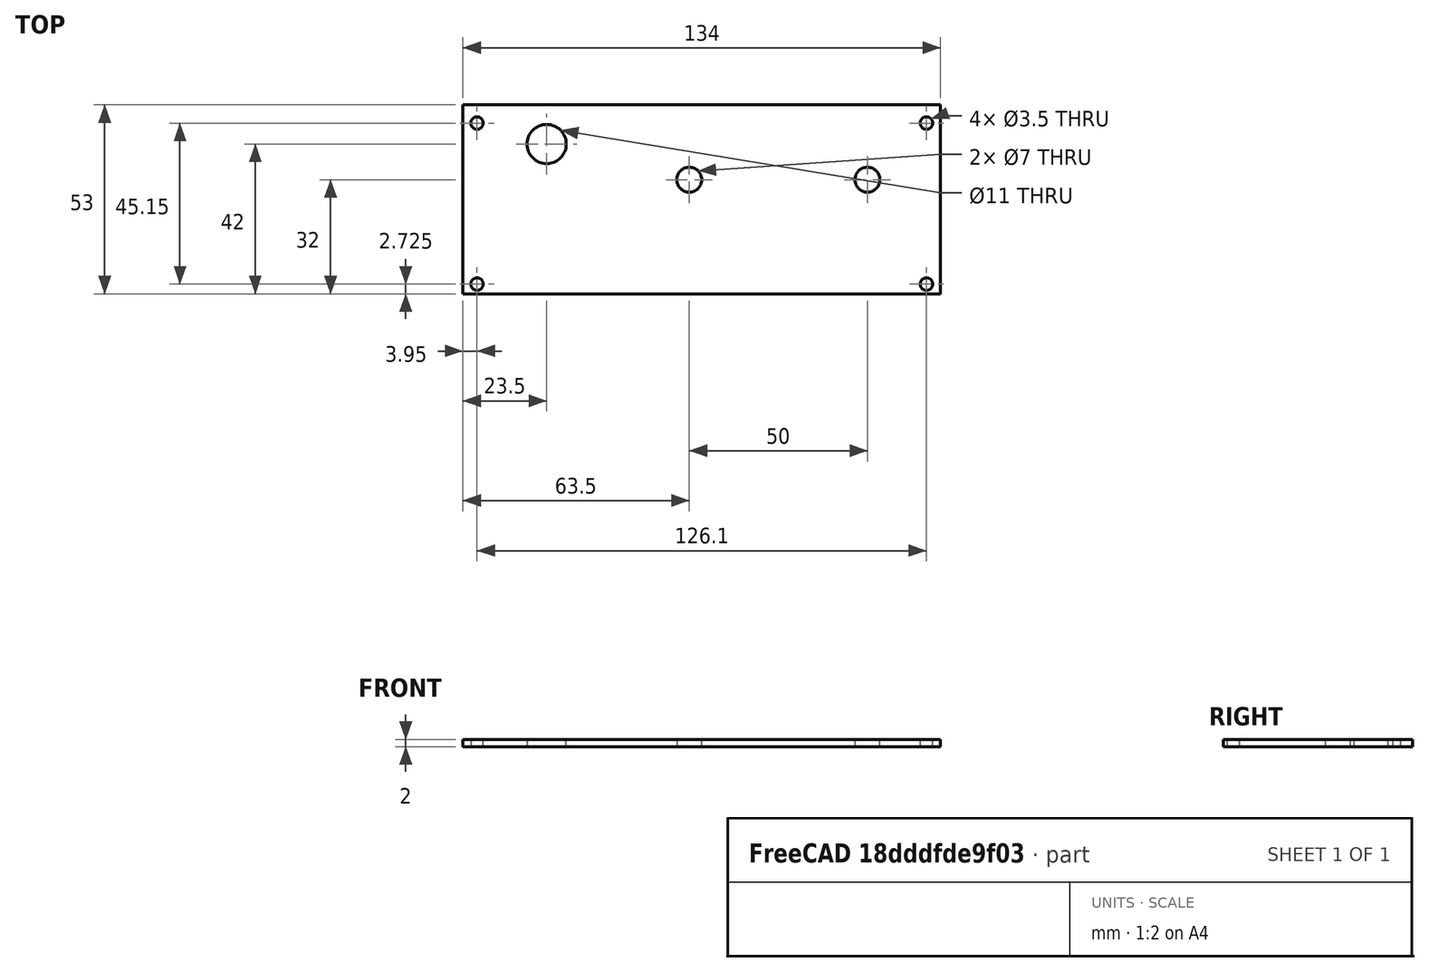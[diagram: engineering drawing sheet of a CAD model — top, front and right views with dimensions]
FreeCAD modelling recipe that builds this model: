
FCSTD DOCUMENT  (FreeCAD 0.20RUnknown)
Label: 端面
License: All rights reserved
LicenseURL: http://en.wikipedia.org/wiki/All_rights_reserved
objects: Sketcher::SketchObject×1, PartDesign::Pad×1, PartDesign::Body×1, TechDraw::DrawSVGTemplate×1, TechDraw::DrawViewPart×1, TechDraw::DrawPage×1
note: 4 computed .brp shape members not serialized (recipe doc carries the construction recipe); baked Part::Feature solids carry a one-line shape summary decoded from their .brp

FEATURE [Sketcher::SketchObject] Sketch
  FullyConstrained = true
  MapMode = 5
  Support = -> [XY_Plane]
  sketch-geometry (35):
    g0: LineSegment StartX=0 StartY=0 StartZ=0 EndX=134 EndY=0 EndZ=0
    g1: LineSegment StartX=134 StartY=0 StartZ=0 EndX=134 EndY=53 EndZ=0
    g2: LineSegment StartX=134 StartY=53 StartZ=0 EndX=0 EndY=53 EndZ=0
    g3: LineSegment StartX=0 StartY=53 StartZ=0 EndX=0 EndY=0 EndZ=0
    g4: LineSegment StartX=2 StartY=0 StartZ=0 EndX=132 EndY=0 EndZ=0
    g5: LineSegment StartX=132 StartY=0 StartZ=0 EndX=132 EndY=50.6 EndZ=0
    g6: LineSegment StartX=132 StartY=50.6 StartZ=0 EndX=2 EndY=50.6 EndZ=0
    g7: LineSegment StartX=2 StartY=50.6 StartZ=0 EndX=2 EndY=0 EndZ=0
    g8: LineSegment StartX=2 StartY=50.6 StartZ=0 EndX=5.9 EndY=50.6 EndZ=0
    g9: LineSegment StartX=5.9 StartY=50.6 StartZ=0 EndX=5.9 EndY=45.15 EndZ=0
    g10: LineSegment StartX=2 StartY=45.15 StartZ=0 EndX=2 EndY=50.6 EndZ=0
    g11: LineSegment StartX=132 StartY=50.6 StartZ=0 EndX=128.1 EndY=50.6 EndZ=0
    g12: LineSegment StartX=128.1 StartY=50.6 StartZ=0 EndX=128.1 EndY=45.15 EndZ=0
    g13: LineSegment StartX=128.1 StartY=45.15 StartZ=0 EndX=132 EndY=45.15 EndZ=0
    g14: LineSegment StartX=132 StartY=45.15 StartZ=0 EndX=132 EndY=50.6 EndZ=0
    g15: LineSegment StartX=132 StartY=0 StartZ=0 EndX=128.1 EndY=0 EndZ=0
    g16: LineSegment StartX=128.1 StartY=0 StartZ=0 EndX=128.1 EndY=5.45 EndZ=0
    g17: LineSegment StartX=128.1 StartY=5.45 StartZ=0 EndX=132 EndY=5.45 EndZ=0
    g18: LineSegment StartX=132 StartY=5.45 StartZ=0 EndX=132 EndY=0 EndZ=0
    g19: LineSegment StartX=2 StartY=0 StartZ=0 EndX=5.9 EndY=0 EndZ=0
    g20: LineSegment StartX=5.9 StartY=0 StartZ=0 EndX=5.9 EndY=5.45 EndZ=0
    g21: LineSegment StartX=5.9 StartY=5.45 StartZ=0 EndX=2 EndY=5.45 EndZ=0
    g22: LineSegment StartX=2 StartY=5.45 StartZ=0 EndX=2 EndY=0 EndZ=0
    g23: GeomPoint X=3.95 Y=47.875 Z=0
    g24: GeomPoint X=3.95 Y=2.725 Z=0
    g25: GeomPoint X=130.05 Y=47.875 Z=0
    g26: GeomPoint X=130.05 Y=2.725 Z=0
    g27: Circle CenterX=3.95 CenterY=47.875 CenterZ=0 NormalX=0 NormalY=0 NormalZ=1 AngleXU=0 Radius=1.75
    g28: Circle CenterX=3.95 CenterY=2.725 CenterZ=0 NormalX=0 NormalY=0 NormalZ=1 AngleXU=0 Radius=1.75
    g29: Circle CenterX=130.05 CenterY=2.725 CenterZ=0 NormalX=0 NormalY=0 NormalZ=1 AngleXU=0 Radius=1.75
    g30: Circle CenterX=130.05 CenterY=47.875 CenterZ=0 NormalX=0 NormalY=0 NormalZ=1 AngleXU=0 Radius=1.75
    g31: Circle CenterX=113.5 CenterY=32 CenterZ=0 NormalX=0 NormalY=0 NormalZ=1 AngleXU=0 Radius=3.5
    g32: Circle CenterX=63.5 CenterY=32 CenterZ=0 NormalX=0 NormalY=0 NormalZ=1 AngleXU=0 Radius=3.5
    g33: Circle CenterX=23.5 CenterY=42 CenterZ=0 NormalX=0 NormalY=0 NormalZ=1 AngleXU=0 Radius=5.5
    g34: LineSegment StartX=2 StartY=45.15 StartZ=0 EndX=5.9 EndY=45.15 EndZ=0
  constraints (88):
    c: Coincident(g0,g1)
    c: Coincident(g1,g2)
    c: Coincident(g2,g3)
    c: Coincident(g3,g0)
    c: Horizontal(g0)
    c: Horizontal(g2)
    c: Vertical(g1)
    c: Vertical(g3)
    c: Coincident(g0,g-1)
    c: DistanceX(g2,g2) = 134
    c: DistanceY(g3,g3) = 53
    c: Coincident(g4,g5)
    c: Coincident(g5,g6)
    c: Coincident(g6,g7)
    c: Coincident(g7,g4)
    c: Horizontal(g4)
    c: Horizontal(g6)
    c: Vertical(g5)
    c: Vertical(g7)
    c: DistanceY(g5,g1) = 2.4
    c: DistanceX(g5,g1) = 2
    c: DistanceX(g2,g6) = 2
    c: PointOnObject(g4,g0)
    c: Coincident(g8,g9)
    c: Coincident(g10,g8)
    c: Horizontal(g8)
    c: Vertical(g9)
    c: Vertical(g10)
    c: Coincident(g8,g6)
    c: Coincident(g11,g12)
    c: Coincident(g12,g13)
    c: Coincident(g13,g14)
    c: Coincident(g14,g11)
    c: Horizontal(g11)
    c: Horizontal(g13)
    c: Vertical(g12)
    c: Vertical(g14)
    c: Coincident(g11,g5)
    c: Coincident(g15,g16)
    c: Coincident(g16,g17)
    c: Coincident(g17,g18)
    c: Coincident(g18,g15)
    c: Horizontal(g15)
    c: Horizontal(g17)
    c: Vertical(g16)
    c: Vertical(g18)
    c: Coincident(g15,g4)
    c: Coincident(g19,g20)
    c: Coincident(g20,g21)
    c: Coincident(g21,g22)
    c: Coincident(g22,g19)
    c: Horizontal(g19)
    c: Horizontal(g21)
    c: Vertical(g20)
    c: Vertical(g22)
    c: Coincident(g19,g4)
    c: Vertical(g9,g20)
    c: Vertical(g12,g16)
    c: Equal(g9,g20)
    c: Equal(g12,g16)
    c: Equal(g17,g21)
    c: Horizontal(g9,g12)
    c: DistanceX(g9,g12) = 122.2
    c: DistanceY(g20,g9) = 39.7
    c: Symmetric(g6,g9,g23)
    c: Symmetric(g20,g4,g24)
    c: Symmetric(g5,g12,g25)
    c: Symmetric(g16,g4,g26)
    c: Coincident(g27,g23)
    c: Coincident(g28,g24)
    c: Coincident(g29,g26)
    c: Coincident(g30,g25)
    c: Equal(g30,g29)
    c: Equal(g29,g28)
    c: Equal(g28,g27)
    c: Diameter(g27) = 3.5
    c: DistanceY(g31,g1) = 21
    c: DistanceX(g31,g0) = 20.5
    c: Diameter(g31) = 7
    c: Horizontal(g32,g31)
    c: DistanceX(g32,g31) = 50
    c: Diameter(g32) = 7
    c: Diameter(g33) = 11
    c: DistanceY(g32,g33) = 10
    c: DistanceX(g33,g32) = 40
    c: Coincident(g34,g10)
    c: Coincident(g34,g9)
    c: Horizontal(g34)
FEATURE [PartDesign::Pad] Pad
  Direction = (0,0,1)
  Length = 2
  Length2 = 10
  Profile = -> Sketch
  ReferenceAxis = -> Sketch [N_Axis]
  Type = 0
FEATURE [PartDesign::Body] Body
  Group = -> [Sketch,Pad]
  Origin = -> Origin
  Tip = -> Pad
FEATURE [TechDraw::DrawSVGTemplate] Template
  EditableTexts = Designed_by_Name=Designed by Name; Drawing_number=Drawing number; FC-Date=Date; FC-SC=Scale; FC-SH=Sheet; FC-Title=Title; Subtitle=Subtitle; Weight=Weight
  Height = 210
  Orientation = 1
  Width = 297
FEATURE [TechDraw::DrawViewPart] View
  CoarseView = false
  Direction = (0,0,1)
  Focus = 100
  HardHidden = false
  IsoCount = 0
  IsoHidden = false
  IsoVisible = false
  LockPosition = false
  Perspective = false
  Rotation = 0
  ScaleType = 0
  SeamHidden = false
  SeamVisible = true
  SmoothHidden = false
  SmoothVisible = true
  Source = -> [Pad]
  X = 148.5
  XDirection = (1,0,0)
  Y = 105
FEATURE [TechDraw::DrawPage] Page
  KeepUpdated = true
  NextBalloonIndex = 1
  ProjectionType = 0
  Template = -> Template
  Views = -> [View]
